# Revit family: Shower-Drain-Waterworks-Universal
name_source: partatom
category: Pipe Accessories
revit_build: Autodesk Revit MEP 2014 (Build: 20140709_2115(x64)
units: mm (PartAtom-declared; Revit-internal decimal feet)

## types (17) — shared parameters
Alt Finish = Metal - Waterworks - Unfinished
Assembly Code = D2010
Certification IAPMO = Yes
Certification State of MA = Yes
Certification cUPC = Yes
Code Compliance = Code # WWSD02: ASME A112.18.2 / CSA B125.2, IAPMO, State of MA
Default Elevation = 0' - 0"
Depth = 0' - 8 3/8"
Drain Hole Diameter = 0' - 2"
Height = 0' - 5"
Keynote = 22 40 00
Label = FD
Length = 0' - 8 3/8"
Manufacturer = Waterworks
Model = UNSD02
Outlet Connection Diameter = 0' - 2"
Outlet Connection Typer = Outlet - No Hub
Product Documentation Link = http://assets.waterworks.com
Product Page URL = http://www.waterworks.com
URL = http://www.waterworks.com
Version = 2014 - v1.0a
Warranty = http://www.waterworks.com
‌Installation Requirements or Notes = This single drain can handle 17 gpm

## per-type parameters (varying)
| type | Constraint | Description | Finish | Model SKU | Product Name |
| Antique Brass | 1 | Universal Shower Drain in Antique Brass | Metal - Waterworks - Antique Brass | 26-57959-24091 | Universal Shower Drain in Antique Brass |
| Antique Copper | 2 | Universal Shower Drain in Antique Copper | Metal - Waterworks - Antique Copper | 26-15307-98342 | Universal Shower Drain in Antique Copper |
| Architectural Bronze | 3 | Universal Shower Drain in Architectural Bronze | Metal - Waterworks - Architectural Bronze | 26-35005-59774 | Universal Shower Drain in Architectural Bronze |
| Burnished Brass | 4 | Universal Shower Drain in Burnished Brass | Metal - Waterworks - Burnished Brass | 26-75946-93689 | Universal Shower Drain in Burnished Brass |
| Burnished Nickel | 5 | Universal Shower Drain in Burnished Nickel | Metal - Waterworks - Burnished Nickel | 26-46664-78511 | Universal Shower Drain in Burnished Nickel |
| Carbon | 6 | Universal Shower Drain in Carbon | Metal - Waterworks - Carbon | 26-10276-80081 | Universal Shower Drain in Carbon |
| Chrome | 7 | Universal Shower Drain in Chrome | Metal - Waterworks - Chrome | 26-84778-17046 | Universal Shower Drain in Chrome |
| Gold | 8 | Universal Shower Drain in Gold | Metal - Waterworks - Gold | 26-79254-35075 | Universal Shower Drain in Gold |
| Graphite | 9 | Universal Shower Drain in Graphite | Metal - Waterworks - Graphite | 26-63643-85030 | Universal Shower Drain in Graphite |
| Matte Gold | 10 | Universal Shower Drain in Matte Gold | Metal - Waterworks - Matte Gold | 26-84421-61040 | Universal Shower Drain in Matte Gold |
| Matte Nickel | 11 | Universal Shower Drain in Matte Nickel | Metal - Waterworks - Matte Nickel | 26-19734-27541 | Universal Shower Drain in Matte Nickel |
| Nickel | 12 | Universal Shower Drain in Nickel | Metal - Waterworks - Nickel | 26-70824-72408 | Universal Shower Drain in Nickel |
| Pewter | 13 | Universal Shower Drain in Pewter | Metal - Waterworks - Pewter | 26-83240-41358 | Universal Shower Drain in Pewter |
| Shiny Copper | 14 | Universal Shower Drain in Shiny Copper | Metal - Waterworks - Shiny Copper | 26-04110-14663 | Universal Shower Drain in Shiny Copper |
| Sovereign | 15 | Universal Shower Drain in Sovereign | Metal - Waterworks - Sovereign | 26-74515-37982 | Universal Shower Drain in Sovereign |
| Unlacquered Brass | 16 | Universal Shower Drain in Unlacquered Brass | Metal - Waterworks - Unlacquered Brass | 26-76117-98440 | Universal Shower Drain in Unlacquered Brass |
| Vintage Brass | 17 | Universal Shower Drain in Vintage Brass | Metal - Waterworks - Vintage Brass | 26-13045-06230 | Universal Shower Drain in Vintage Brass |

## geometry (parser evidence)
native form markers: Sweep x2
no freeform markers — native parametric forms only
